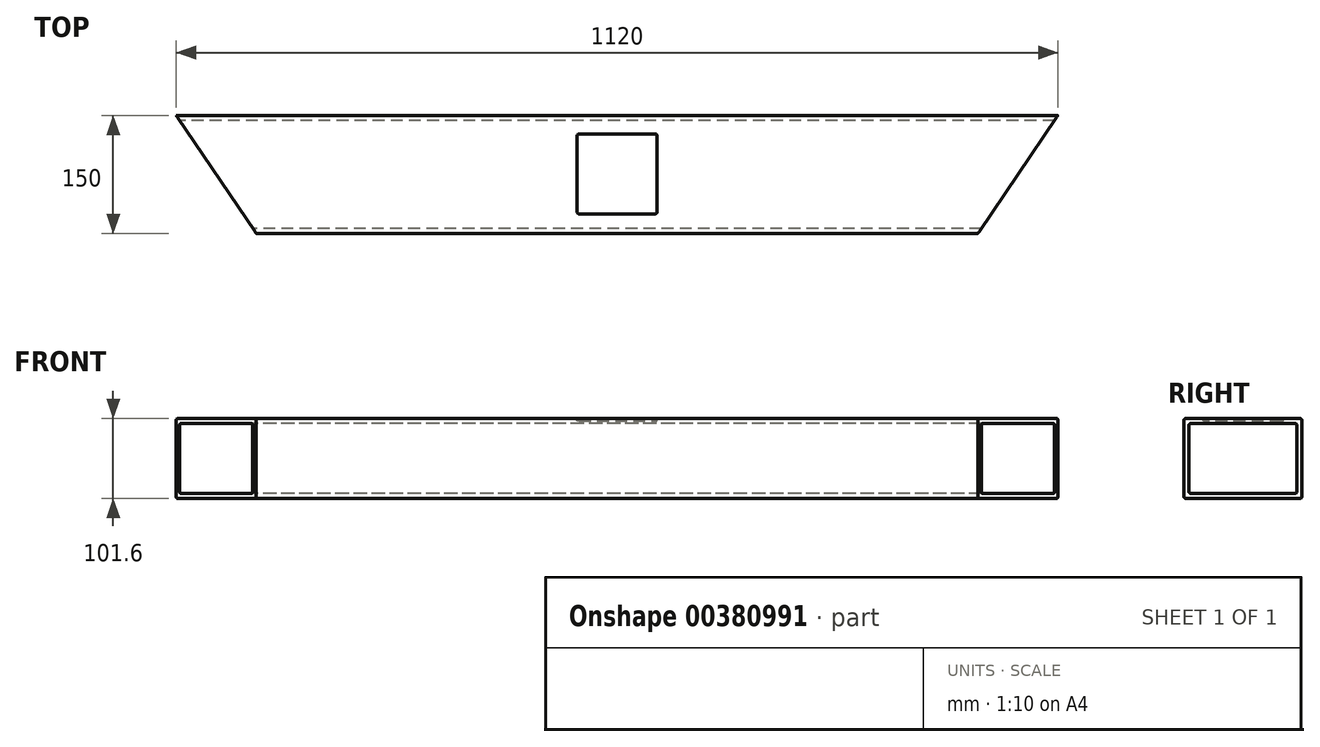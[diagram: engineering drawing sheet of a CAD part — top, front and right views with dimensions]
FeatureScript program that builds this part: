
annotation { "Feature Type Name" : "Feature", "Feature Type Description" : "" }
export const myFeature = defineFeature(function(context is Context, id is Id, definition is map)
    precondition{}
    {
        {
            var Q0;
            Q0=qCreatedBy(makeId("Top.planeOp"),FACE);
            var sketch = newSketch(context, id + "F0", { "sketchPlane" : qUnion([Q0])});
            skLineSegment(sketch, "E0.bottom", {"start": v(560, 75) * mm, "end": v(-560, 75) * mm});
            skLineSegment(sketch, "E0.top", {"start": v(560, -75) * mm, "end": v(-560, -75) * mm});
            skLineSegment(sketch, "E0.left", {"start": v(560, 75) * mm, "end": v(560, -75) * mm});
            skLineSegment(sketch, "E0.right", {"start": v(-560, 75) * mm, "end": v(-560, -75) * mm});
            skPoint(sketch, "E0.middle", {"position": v(0, 0) * mm});
            skSolve(sketch);
        }
        {
            var Q0;
            Q0=makeQuery(id+"F0.imprint","IMPRINT",FACE,{"disambiguationData":[TD([[makeQuery(id+"F0.imprint","IMPRINT",EDGE,{"derivedFrom":sQuery(id+"F0.wireOp",EDGE,"E0.bottom")}),1.0]])]});
            extrude(context, id + "F1", {"entities" : qUnion([Q0]), "endBound" : BoundingType.SYMMETRIC, "depth" : 101.6 * mm});
        }
        {
            var Q0;
            Q0=makeQuery(id+"F1.opExtrude","SWEPT_FACE",FACE,{"disambiguationData":[OSD([sQuery(id+"F0.wireOp",EDGE,"E0.right")])]});
            var sketch = newSketch(context, id + "F2", { "sketchPlane" : qUnion([Q0])});
            skLineSegment(sketch, "E1.bottom", {"start": v(68.65, 44.45) * mm, "end": v(-68.65, 44.45) * mm});
            skLineSegment(sketch, "E1.top", {"start": v(68.65, -44.45) * mm, "end": v(-68.65, -44.45) * mm});
            skLineSegment(sketch, "E1.left", {"start": v(68.65, 44.45) * mm, "end": v(68.65, -44.45) * mm});
            skLineSegment(sketch, "E1.right", {"start": v(-68.65, 44.45) * mm, "end": v(-68.65, -44.45) * mm});
            skPoint(sketch, "E1.middle", {"position": v(0, 0) * mm});
            skLineSegment(sketch, "E2", {"start": v(75, 50) * mm, "end": v(75, -50) * mm});
            skLineSegment(sketch, "E3", {"start": v(-75, 50.8) * mm, "end": v(75, 50.8) * mm});
            skLineSegment(sketch, "E4", {"start": v(-75, 50) * mm, "end": v(-75, -50) * mm});
            skLineSegment(sketch, "E5", {"start": v(-75, -50.8) * mm, "end": v(75, -50.8) * mm});
            skSolve(sketch);
        }
        {
            var Q0;
            Q0=makeQuery(id+"F2.imprint","IMPRINT",FACE,{"disambiguationData":[TD([[makeQuery(id+"F2.imprint","IMPRINT",EDGE,{"derivedFrom":sQuery(id+"F2.wireOp",EDGE,"E1.bottom")}),1.0]])]});
            extrude(context, id + "F3", {"entities" : qUnion([Q0]), "operationType" : NewBodyOperationType.REMOVE, "endBound" : BoundingType.UP_TO_NEXT, "oppositeDirection" : true, "depth" : 25 * mm});
        }
        {
            var Q0;
            Q0=makeQuery(id+"F1.opExtrude","CAP_FACE",FACE,{"disambiguationData":[OSD([sQuery(id+"F0.wireOp",EDGE,"E0.bottom"),sQuery(id+"F0.wireOp",EDGE,"E0.top"),sQuery(id+"F0.wireOp",EDGE,"E0.left"),sQuery(id+"F0.wireOp",EDGE,"E0.right")])],"isStart":false});
            var sketch = newSketch(context, id + "F4", { "sketchPlane" : qUnion([Q0])});
            skLineSegment(sketch, "E6", {"start": v(560, -75) * mm, "end": v(458.4, -75) * mm});
            skLineSegment(sketch, "E7", {"start": v(458.4, -75) * mm, "end": v(560, 75) * mm});
            skLineSegment(sketch, "E8", {"start": v(560, 75) * mm, "end": v(560, -75) * mm});
            skSolve(sketch);
        }
        {
            var Q0;
            Q0=makeQuery(id+"F4.imprint","IMPRINT",FACE,{"disambiguationData":[TD([[makeQuery(id+"F4.imprint","IMPRINT",EDGE,{"derivedFrom":sQuery(id+"F4.wireOp",EDGE,"E6")}),-1.0]])]});
            extrude(context, id + "F5", {"entities" : qUnion([Q0]), "operationType" : NewBodyOperationType.REMOVE, "endBound" : BoundingType.THROUGH_ALL, "oppositeDirection" : true, "depth" : 25 * mm});
        }
        {
            var Q0;
            Q0=makeQuery(id+"F1.opExtrude","CAP_FACE",FACE,{"disambiguationData":[OSD([sQuery(id+"F0.wireOp",EDGE,"E0.bottom"),sQuery(id+"F0.wireOp",EDGE,"E0.top"),sQuery(id+"F0.wireOp",EDGE,"E0.left"),sQuery(id+"F0.wireOp",EDGE,"E0.right")])],"isStart":false});
            var sketch = newSketch(context, id + "F6", { "sketchPlane" : qUnion([Q0])});
            skLineSegment(sketch, "E9", {"start": v(-560, -75) * mm, "end": v(-458.4, -75) * mm});
            skLineSegment(sketch, "E10", {"start": v(-458.4, -75) * mm, "end": v(-560, 75) * mm});
            skLineSegment(sketch, "E11", {"start": v(-560, 75) * mm, "end": v(-560, -75) * mm});
            skSolve(sketch);
        }
        {
            var Q0;
            Q0=makeQuery(id+"F6.imprint","IMPRINT",FACE,{"disambiguationData":[TD([[makeQuery(id+"F6.imprint","IMPRINT",EDGE,{"derivedFrom":sQuery(id+"F6.wireOp",EDGE,"E9")}),-1.0]])]});
            extrude(context, id + "F7", {"entities" : qUnion([Q0]), "operationType" : NewBodyOperationType.REMOVE, "endBound" : BoundingType.THROUGH_ALL, "oppositeDirection" : true, "depth" : 25 * mm});
        }
        {
            var Q0;
            Q0=makeQuery(id+"F1.opExtrude","CAP_EDGE",EDGE,{"disambiguationData":[OSD([sQuery(id+"F0.wireOp",EDGE,"E0.top")])],"isStart":false});
            var Q1;
            Q1=makeQuery(id+"F1.opExtrude","CAP_EDGE",EDGE,{"disambiguationData":[OSD([sQuery(id+"F0.wireOp",EDGE,"E0.top")])],"isStart":true});
            var Q2;
            Q2=makeQuery(id+"F1.opExtrude","CAP_EDGE",EDGE,{"disambiguationData":[OSD([sQuery(id+"F0.wireOp",EDGE,"E0.bottom")])],"isStart":true});
            var Q3;
            Q3=makeQuery(id+"F1.opExtrude","CAP_EDGE",EDGE,{"disambiguationData":[OSD([sQuery(id+"F0.wireOp",EDGE,"E0.bottom")])],"isStart":false});
            var Q4;
            Q4=makeQuery(id+"F3.boolean.opBoolean","COPY",EDGE,{"derivedFrom":makeQuery(id+"F3.opExtrude","SWEPT_EDGE",EDGE,{"disambiguationData":[OSD([sQuery(id+"F2.wireOp",EDGE,"E1.top"),sQuery(id+"F2.wireOp",EDGE,"E1.right")])]})});
            var Q5;
            Q5=makeQuery(id+"F3.boolean.opBoolean","COPY",EDGE,{"derivedFrom":makeQuery(id+"F3.opExtrude","SWEPT_EDGE",EDGE,{"disambiguationData":[OSD([sQuery(id+"F2.wireOp",EDGE,"E1.bottom"),sQuery(id+"F2.wireOp",EDGE,"E1.right")])]})});
            var Q6;
            Q6=makeQuery(id+"F3.boolean.opBoolean","COPY",EDGE,{"derivedFrom":makeQuery(id+"F3.opExtrude","SWEPT_EDGE",EDGE,{"disambiguationData":[OSD([sQuery(id+"F2.wireOp",EDGE,"E1.bottom"),sQuery(id+"F2.wireOp",EDGE,"E1.left")])]})});
            var Q7;
            Q7=makeQuery(id+"F3.boolean.opBoolean","COPY",EDGE,{"derivedFrom":makeQuery(id+"F3.opExtrude","SWEPT_EDGE",EDGE,{"disambiguationData":[OSD([sQuery(id+"F2.wireOp",EDGE,"E1.top"),sQuery(id+"F2.wireOp",EDGE,"E1.left")])]})});
            fillet(context, id + "F8", {"entities" : qUnion([Q0, Q1, Q2, Q3, Q4, Q5, Q6, Q7]), "radius" : 2.4 * mm, "tangentPropagation" : true, "allowEdgeOverflow" : false});
        }
        {
            var Q0;
            Q0=makeQuery(id+"F1.opExtrude","CAP_FACE",FACE,{"disambiguationData":[OSD([sQuery(id+"F0.wireOp",EDGE,"E0.bottom"),sQuery(id+"F0.wireOp",EDGE,"E0.top"),sQuery(id+"F0.wireOp",EDGE,"E0.left"),sQuery(id+"F0.wireOp",EDGE,"E0.right")])],"isStart":false});
            var sketch = newSketch(context, id + "F9", { "sketchPlane" : qUnion([Q0])});
            skLineSegment(sketch, "E12.bottom", {"start": v(-50.8, 51.6) * mm, "end": v(50.8, 51.6) * mm});
            skLineSegment(sketch, "E12.top", {"start": v(-50.8, -50) * mm, "end": v(50.8, -50) * mm});
            skLineSegment(sketch, "E12.left", {"start": v(-50.8, 51.6) * mm, "end": v(-50.8, -50) * mm});
            skLineSegment(sketch, "E12.right", {"start": v(50.8, 51.6) * mm, "end": v(50.8, -50) * mm});
            skSolve(sketch);
        }
        {
            var Q0;
            Q0=makeQuery(id+"F9.imprint","IMPRINT",FACE,{"disambiguationData":[TD([[makeQuery(id+"F9.imprint","IMPRINT",EDGE,{"derivedFrom":sQuery(id+"F9.wireOp",EDGE,"E12.bottom")}),-1.0]])]});
            extrude(context, id + "F10", {"entities" : qUnion([Q0]), "operationType" : NewBodyOperationType.REMOVE, "oppositeDirection" : true, "depth" : 3.17 * mm});
        }
        {
            var Q0;
            Q0=makeQuery(id+"F10.boolean.opBoolean","COPY",EDGE,{"derivedFrom":makeQuery(id+"F10.opExtrude","SWEPT_EDGE",EDGE,{"disambiguationData":[OSD([sQuery(id+"F9.wireOp",EDGE,"E12.bottom"),sQuery(id+"F9.wireOp",EDGE,"E12.right")])]})});
            var Q1;
            Q1=makeQuery(id+"F10.boolean.opBoolean","COPY",EDGE,{"derivedFrom":makeQuery(id+"F10.opExtrude","SWEPT_EDGE",EDGE,{"disambiguationData":[OSD([sQuery(id+"F9.wireOp",EDGE,"E12.top"),sQuery(id+"F9.wireOp",EDGE,"E12.right")])]})});
            var Q2;
            Q2=makeQuery(id+"F10.boolean.opBoolean","COPY",EDGE,{"derivedFrom":makeQuery(id+"F10.opExtrude","SWEPT_EDGE",EDGE,{"disambiguationData":[OSD([sQuery(id+"F9.wireOp",EDGE,"E12.top"),sQuery(id+"F9.wireOp",EDGE,"E12.left")])]})});
            var Q3;
            Q3=makeQuery(id+"F10.boolean.opBoolean","COPY",EDGE,{"derivedFrom":makeQuery(id+"F10.opExtrude","SWEPT_EDGE",EDGE,{"disambiguationData":[OSD([sQuery(id+"F9.wireOp",EDGE,"E12.bottom"),sQuery(id+"F9.wireOp",EDGE,"E12.left")])]})});
            fillet(context, id + "F11", {"entities" : qUnion([Q0, Q1, Q2, Q3]), "radius" : 2.5 * mm, "tangentPropagation" : true, "allowEdgeOverflow" : false});
        }
    });
